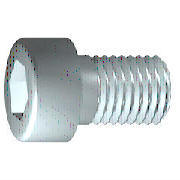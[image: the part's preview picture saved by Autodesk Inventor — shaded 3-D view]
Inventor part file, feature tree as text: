
AUTODESK INVENTOR PART (.ipt)
format: ipt  version: 2023.3 (Build 273359000, 359)  size: 189,952 bytes
history: native  units: mm (DEFAULTED — no unit token found)
features: sketch x2, other x1, extrude x1, plane x1, fillet x1
ambient origin geometry x7: Origin, YZ Plane, XY Plane, X Axis, Y Axis, Z Axis, Center Point
bodies: Solid1 (feature_tree)
feature tree (6):
  other  "Körper"
  extrude  "Loch"  Depth=3.0mm
  plane  "Work Plane1"
  fillet  "Fillet2"  Radius=3.0mm
  sketch  "Skizze1"  dims[d1=14.75mm d2=0.306825mm d3=3.0mm]
  sketch  "Skizze2"  dims[d4=1.3mm d5=60.0deg d6=3.0mm d7=3.0mm d8=2.886751mm d9=5.5mm d10=90.0deg d11=10.0mm d12=0.0mm d13=14.75mm d14=0.0mm d15=0.306725mm d16=0.306725mm d17=0.3mm d19=0.0mm d26=16.0mm d27=45.0deg d28=0.0mm d29=0.0mm d30=0.1mm]
